# Revit family: Layout-Teknion-TBBPAK14-Bene_Package_14-R2016
name_source: partatom
category: Furniture Systems
revit_build: Autodesk Revit Architecture 2016 (Build: 20190507_1515(x64)
units: mm (PartAtom-declared; Revit-internal decimal feet)

## family parameters
Always vertical = Yes
Cut with Voids When Loaded = No
OmniClass Number = 23.40.70.14.64.21
OmniClass Title = Systems Furniture
Part Type = Normal
Room Calculation Point = No
Round Connector Dimension = Use Diameter
Shared = Yes
Work Plane-Based = No

## types (1)
- Bene Package Fourteen
    Assembly Code = E2020200
    Description = Built using Tower Two package: 6 Solid Bene Boxes, 20 Bene Boxes with One Opening, 8 Bene Boxes with Two Openings, 4 Half Bene Boxes, 12 Bene Box Trays, 6 Long Bene Box Trays, 8 Bene Box Tops, 3 Long Bene Box Tops, 10 Bene Box  Seating Pads
    Manufacturer = Teknion
    Manufacturer Fax = 416.661.4586
    Model = Bene Package Fourteen
    Product Documentation Link = https://www.teknion.com
    Product Line = Bene Box
    Product Page URL = https://www.teknionplanningtool.com
    Series = Bene Box
    Sustainability Data = https://www.teknion.com
    URL = www.teknion.com
    Unit Weight URL = http://www.teknion.com
    Warranty = http://www.teknion.com

## geometry (parser evidence)
native form markers: Sweep x29
no freeform markers — native parametric forms only
